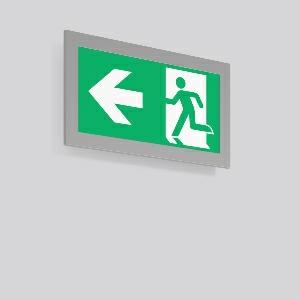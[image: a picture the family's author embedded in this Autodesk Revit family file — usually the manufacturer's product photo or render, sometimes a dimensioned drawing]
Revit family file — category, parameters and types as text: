
# Revit family: tenuo_671944_004_07_24b1
name_source: partatom
category: Lighting Fixtures
units: mm (PartAtom-declared; Revit-internal decimal feet)

## family parameters
Cut with Voids When Loaded = No
Host = Face
Light Source = No
Part Type = Normal
Room Calculation Point = No
Round Connector Dimension = Use Diameter
Shared = No

## types (1)
- TENUO
    Apparent Load = 0 VA
    Default Elevation = 1800 mm
    Description = Series: TENUO
Luminaire for escape route identification. Housing: anodised aluminium, silver. Display panel: patented MicroLens technology and legend on one side. Electronic ballast included. Self-contained system with automatic self-test and feedback via DALI bus, only to RZB DALI monitoring system. Please indicate legend number when placing your order! 
Colour: silver, matt (approx. RAL 9006)
Length: 350 mm
Width: 33 mm
Height: 200 mm
Weight: 1.63 kg
Operating mode: maintained power mode
Viewing Distance: 30 m
Duration time: 3 h
Lamp: LED
Socket: without socket
Colour temperature: 5700K
Colour rendering index (CRI): 80
System power: 4.8 W
System power, emergency: -
Control gear: EB
Protection class: I
Type of protection: IP 40
    Height = 200 mm  [stored 0.656168 ft]
    Lamp = 0 x
    Length = 350 mm
    Luminous efficacy = 0 lm/W
    Manufacturer = RZB
    ModVariant = No
    Model = 671944.004.07
    Mounting Place = Wall
    Mounting Type = Surface mounted
    Number of Poles = 1
    OnlyDefault = Yes
    Power Factor = 1
    Product Name = TENUO
    Product group = Surface mounted Wall luminaires
    ProductGroupID = 2001
    Protection Class = Protection class I
    Protection Degree = IP 40
    RLX_Detail_Level = 1
    RLX_Emergency_Light_Flux = 0 lm
    RLX_Emergency_Type = 0
    RLX_Emergency_Type_DB = No
    RlxData = <blob elided: 28045 chars, md5=7ca878f4>
    Standby Power = 0 W
    System Light Flux = 0 lm
    System Power = 0 W
    Type Comments = ALEA SPOT
    Type Image = 671944.004.jpg
    URL = http://relux.com
    VarID = ---
    Voltage = 230 V
    Voltage Range = 220-240 V
    Weight = 0.00 kg
    Width = 33 mm

note: [stored X ft] marks values corroborated as IEEE doubles in the binary element streams (Revit-internal decimal feet)

## geometry (parser evidence)
native form markers: Blend x4, Sweep x10
no freeform markers — native parametric forms only
